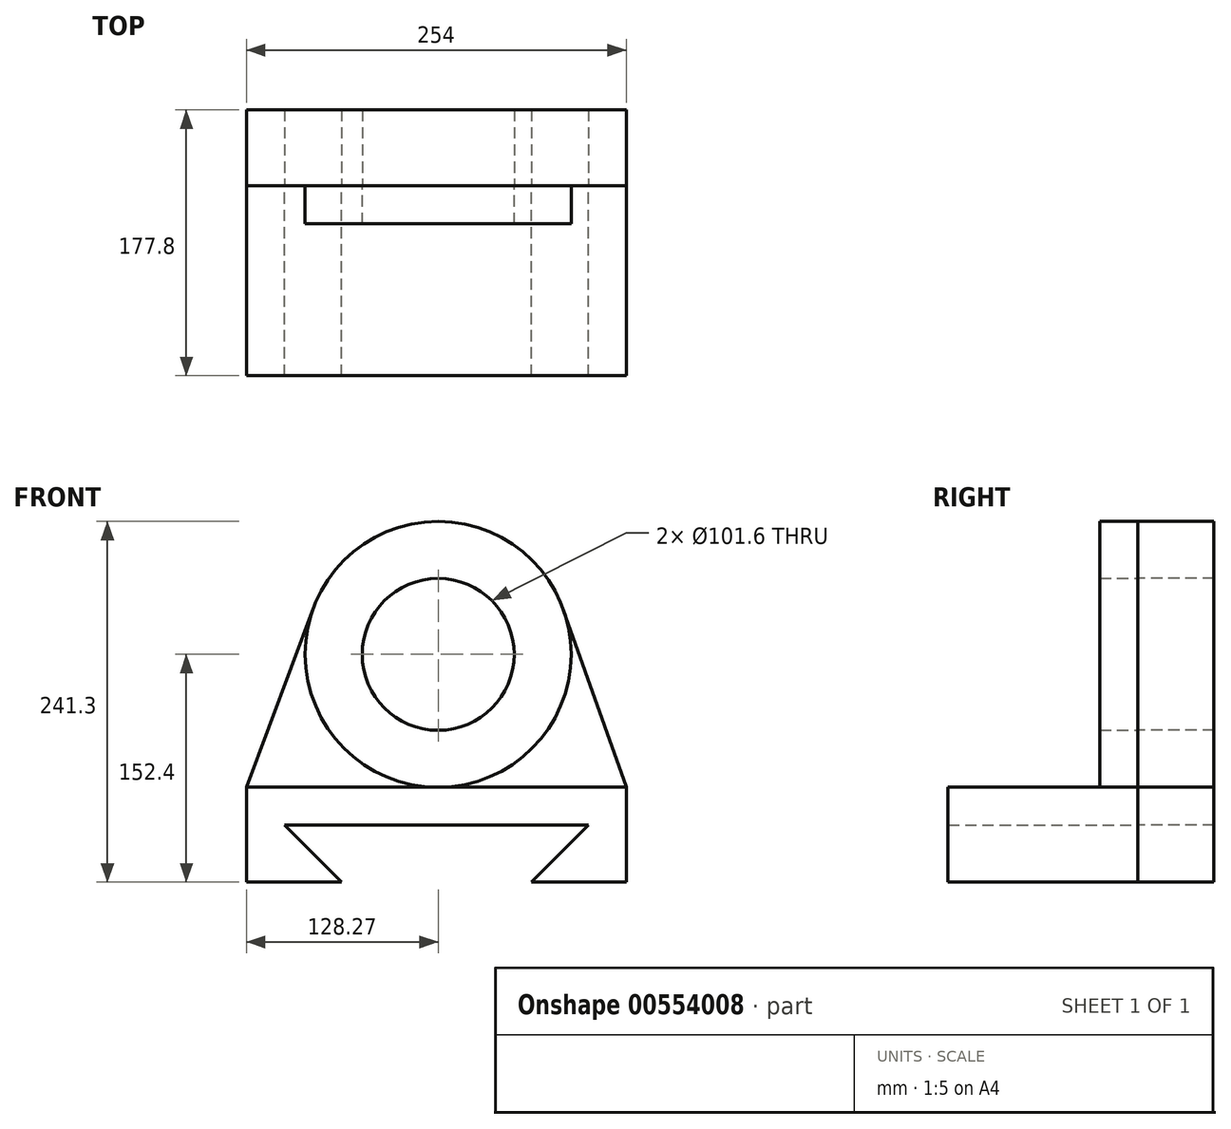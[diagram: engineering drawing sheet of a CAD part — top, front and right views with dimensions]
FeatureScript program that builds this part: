
annotation { "Feature Type Name" : "Feature", "Feature Type Description" : "" }
export const myFeature = defineFeature(function(context is Context, id is Id, definition is map)
    precondition{}
    {
        {
            var Q0;
            Q0=qCreatedBy(makeId("Front.planeOp"),FACE);
            var sketch = newSketch(context, id + "F0", { "sketchPlane" : qUnion([Q0])});
            skLineSegment(sketch, "E0", {"start": v(0, 0) * mm, "end": v(254, 0) * mm});
            skLineSegment(sketch, "E1", {"start": v(254, 0) * mm, "end": v(254, -63.5) * mm});
            skLineSegment(sketch, "E2", {"start": v(254, -63.5) * mm, "end": v(190.5, -63.5) * mm});
            skLineSegment(sketch, "E3", {"start": v(190.5, -63.5) * mm, "end": v(228.6, -25.4) * mm});
            skLineSegment(sketch, "E4", {"start": v(228.6, -25.4) * mm, "end": v(25.4, -25.4) * mm});
            skLineSegment(sketch, "E5", {"start": v(0, 0) * mm, "end": v(0, -63.5) * mm});
            skLineSegment(sketch, "E6", {"start": v(0, -63.5) * mm, "end": v(63.5, -63.5) * mm});
            skLineSegment(sketch, "E7", {"start": v(63.5, -63.5) * mm, "end": v(25.4, -25.4) * mm});
            skCircle(sketch, "E8", {"center": v(128.27, 88.9) * mm, "radius": 88.9 * mm});
            skCircle(sketch, "E9", {"center": v(128.27, 88.9) * mm, "radius": 50.8 * mm});
            skLineSegment(sketch, "E10", {"start": v(0, 0) * mm, "end": v(45.03, 120.1) * mm});
            skLineSegment(sketch, "E11", {"start": v(254, 0) * mm, "end": v(212.08, 118.54) * mm});
            skSolve(sketch);
        }
        {
            var Q0;
            {var subQ0=sQuery(id+"F0.wireOp",EDGE,"E1");Q0=makeQuery(id+"F0.imprint","IMPRINT",FACE,{"disambiguationData":[TD([[makeQuery(id+"F0.imprint","IMPRINT",EDGE,{"derivedFrom":subQ0}),-1.0]])]});}
            extrude(context, id + "F1", {"entities" : qUnion([Q0]), "depth" : 127 * mm, "offsetDistance" : 25.4 * mm});
        }
        {
            var Q0;
            Q0=makeQuery(id+"F0.imprint","IMPRINT",FACE,{"disambiguationData":[TD([[makeQuery(id+"F0.imprint","IMPRINT",EDGE,{"derivedFrom":sQuery(id+"F0.wireOp",EDGE,"E9")}),-1.0]])]});
            extrude(context, id + "F2", {"entities" : qUnion([Q0]), "operationType" : NewBodyOperationType.ADD, "depth" : 25.4 * mm, "offsetDistance" : 25.4 * mm});
        }
        {
            var Q0;
            {var subQ0=sQuery(id+"F0.wireOp",EDGE,"E10");Q0=makeQuery(id+"F0.imprint","IMPRINT",FACE,{"disambiguationData":[TD([[makeQuery(id+"F0.imprint","IMPRINT",EDGE,{"derivedFrom":subQ0}),-1.0]])]});}
            var Q1;
            {var subQ0=sQuery(id+"F0.wireOp",EDGE,"E11");Q1=makeQuery(id+"F0.imprint","IMPRINT",FACE,{"disambiguationData":[TD([[makeQuery(id+"F0.imprint","IMPRINT",EDGE,{"derivedFrom":subQ0}),1.0]])]});}
            var Q2;
            Q2=makeQuery(id+"F0.imprint","IMPRINT",FACE,{"disambiguationData":[TD([[makeQuery(id+"F0.imprint","IMPRINT",EDGE,{"derivedFrom":sQuery(id+"F0.wireOp",EDGE,"E9")}),-1.0]])]});
            var Q3;
            {var subQ0=sQuery(id+"F0.wireOp",EDGE,"E1");Q3=makeQuery(id+"F0.imprint","IMPRINT",FACE,{"disambiguationData":[TD([[makeQuery(id+"F0.imprint","IMPRINT",EDGE,{"derivedFrom":subQ0}),-1.0]])]});}
            extrude(context, id + "F3", {"entities" : qUnion([Q0, Q1, Q2, Q3]), "oppositeDirection" : true, "depth" : 50.8 * mm, "offsetDistance" : 25.4 * mm});
        }
    });
